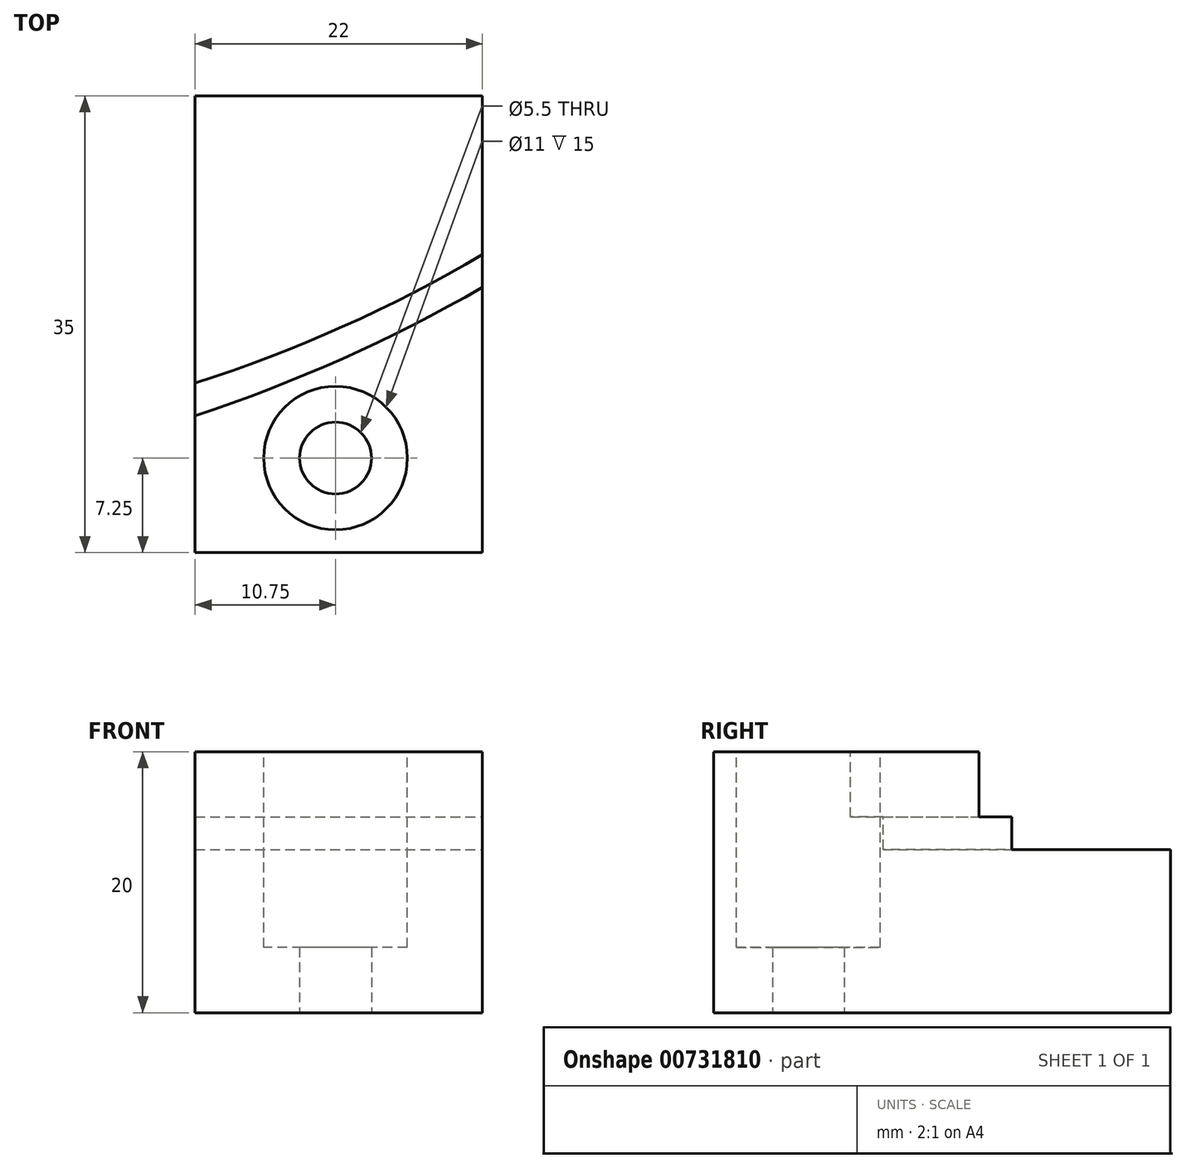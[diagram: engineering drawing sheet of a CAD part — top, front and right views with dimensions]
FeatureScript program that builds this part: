
annotation { "Feature Type Name" : "Feature", "Feature Type Description" : "" }
export const myFeature = defineFeature(function(context is Context, id is Id, definition is map)
    precondition{}
    {
        {
            var Q0;
            Q0=qCreatedBy(makeId("Top.planeOp"),FACE);
            var sketch = newSketch(context, id + "F0", { "sketchPlane" : qUnion([Q0])});
            skLineSegment(sketch, "E0.bottom", {"start": v(-22, 0) * mm, "end": v(0, 0) * mm});
            skLineSegment(sketch, "E0.top", {"start": v(-22, -35) * mm, "end": v(0, -35) * mm});
            skLineSegment(sketch, "E0.left", {"start": v(-22, 0) * mm, "end": v(-22, -35) * mm});
            skLineSegment(sketch, "E0.right", {"start": v(0, 0) * mm, "end": v(0, -35) * mm});
            skCircle(sketch, "E1", {"center": v(-11.25, -27.75) * mm, "radius": 2.75 * mm});
            skSolve(sketch);
        }
        {
            var Q0;
            Q0=qSketchRegion(id+"F0",true);
            extrude(context, id + "F1", {"entities" : qUnion([Q0]), "depth" : 20 * mm});
        }
        {
            var Q0;
            Q0=makeQuery(id+"F1.opExtrude","CAP_FACE",FACE,{"disambiguationData":[OSD([sQuery(id+"F0.wireOp",EDGE,"E0.bottom"),sQuery(id+"F0.wireOp",EDGE,"E0.top"),sQuery(id+"F0.wireOp",EDGE,"E0.left"),sQuery(id+"F0.wireOp",EDGE,"E0.right"),sQuery(id+"F0.wireOp",EDGE,"E1")])],"isStart":false});
            var sketch = newSketch(context, id + "F2", { "sketchPlane" : qUnion([Q0])});
            skCircle(sketch, "E2.0", {"center": v(-11.25, -27.75) * mm, "radius": 2.75 * mm});
            skCircle(sketch, "E3.0", {"center": v(-11.25, -27.75) * mm, "radius": 5.5 * mm});
            skSolve(sketch);
        }
        {
            var Q0;
            Q0=qSketchRegion(id+"F2",true);
            extrude(context, id + "F3", {"entities" : qUnion([Q0]), "operationType" : NewBodyOperationType.REMOVE, "oppositeDirection" : true, "depth" : 15 * mm});
        }
        {
            var Q0;
            Q0=makeQuery(id+"F1.opExtrude","CAP_FACE",FACE,{"disambiguationData":[OSD([sQuery(id+"F0.wireOp",EDGE,"E0.bottom"),sQuery(id+"F0.wireOp",EDGE,"E0.top"),sQuery(id+"F0.wireOp",EDGE,"E0.left"),sQuery(id+"F0.wireOp",EDGE,"E0.right"),sQuery(id+"F0.wireOp",EDGE,"E1")])],"isStart":false});
            var sketch = newSketch(context, id + "F4", { "sketchPlane" : qUnion([Q0])});
            skLineSegment(sketch, "E4.0.0", {"start": v(-22, 0) * mm, "end": v(-22, -35) * mm});
            skLineSegment(sketch, "E4.0.1", {"start": v(-22, -35) * mm, "end": v(0, -35) * mm});
            skLineSegment(sketch, "E4.0.2", {"start": v(0, -35) * mm, "end": v(0, 0) * mm});
            skLineSegment(sketch, "E4.0.3", {"start": v(0, 0) * mm, "end": v(-22, 0) * mm});
            skCircle(sketch, "E5", {"center": v(-59.73, 89.4) * mm, "radius": 120 * mm});
            skSolve(sketch);
        }
        {
            var Q0;
            {var subQ0=sQuery(id+"F4.wireOp",EDGE,"E4.0.3");Q0=makeQuery(id+"F4.imprint","IMPRINT",FACE,{"disambiguationData":[TD([[makeQuery(id+"F4.imprint","IMPRINT",EDGE,{"derivedFrom":subQ0}),-1.0]])]});}
            extrude(context, id + "F5", {"entities" : qUnion([Q0]), "operationType" : NewBodyOperationType.REMOVE, "oppositeDirection" : true, "depth" : 5 * mm});
        }
        {
            var Q0;
            Q0=makeQuery(id+"F5.boolean.opBoolean","COPY",FACE,{"derivedFrom":makeQuery(id+"F5.opExtrude","CAP_FACE",FACE,{"disambiguationData":[OSD([sQuery(id+"F4.wireOp",EDGE,"E4.0.0"),sQuery(id+"F4.wireOp",EDGE,"E4.0.2"),sQuery(id+"F4.wireOp",EDGE,"E4.0.3"),sQuery(id+"F4.wireOp",EDGE,"E5")])],"isStart":false})});
            var sketch = newSketch(context, id + "F6", { "sketchPlane" : qUnion([Q0])});
            skLineSegment(sketch, "E6", {"start": v(-22, 0) * mm, "end": v(-22, -22) * mm});
            skLineSegment(sketch, "E7", {"start": v(0, -12.17) * mm, "end": v(0, 0) * mm});
            skLineSegment(sketch, "E8", {"start": v(0, 0) * mm, "end": v(-22, 0) * mm});
            skArc(sketch, "E9", {"start": v(-22, -22) * mm, "mid": v(-10.73, -17.7) * mm, "end": v(0, -12.17) * mm});
            skSolve(sketch);
        }
        {
            var Q0;
            Q0 = qSketchRegion(id + "F6", true);
            extrude(context, id + "F7", {"entities" : qUnion([Q0]), "operationType" : NewBodyOperationType.REMOVE, "oppositeDirection" : true, "depth" : 2.5 * mm, "offsetDistance" : 25 * mm});
        }
    });
